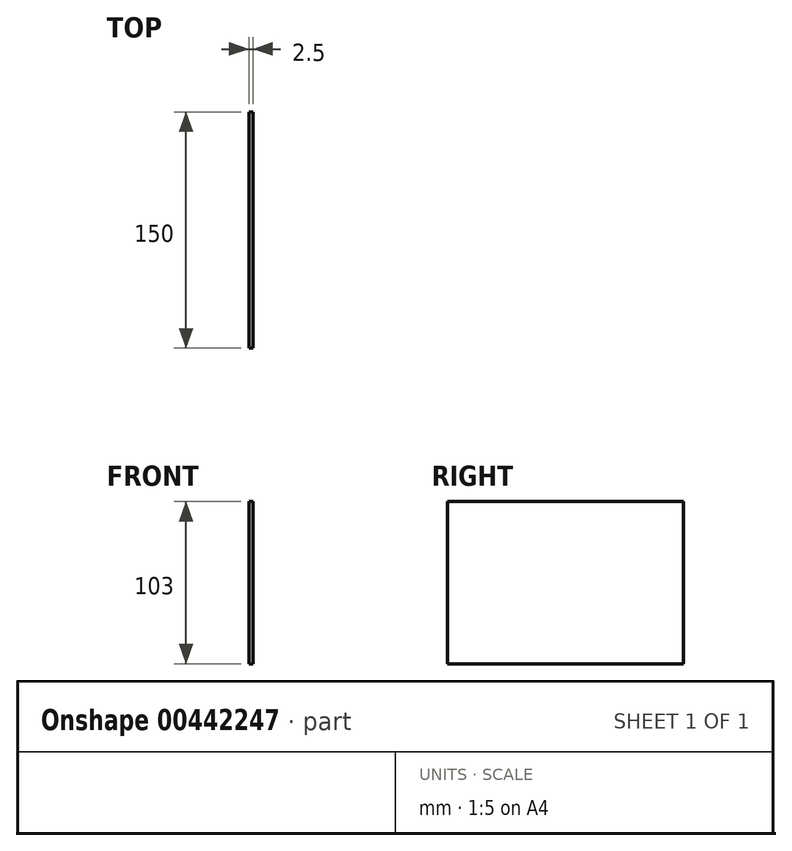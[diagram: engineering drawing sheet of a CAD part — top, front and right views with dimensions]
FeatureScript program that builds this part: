
annotation { "Feature Type Name" : "Feature", "Feature Type Description" : "" }
export const myFeature = defineFeature(function(context is Context, id is Id, definition is map)
    precondition{}
    {
        {
            var Q0;
            Q0=qCreatedBy(makeId("Front.planeOp"),FACE);
            var sketch = newSketch(context, id + "F0", { "sketchPlane" : qUnion([Q0])});
            skLineSegment(sketch, "E0.bottom", {"start": v(-1.25, 51.5) * mm, "end": v(1.25, 51.5) * mm});
            skLineSegment(sketch, "E0.top", {"start": v(-1.25, -51.5) * mm, "end": v(1.25, -51.5) * mm});
            skLineSegment(sketch, "E0.left", {"start": v(-1.25, 51.5) * mm, "end": v(-1.25, -51.5) * mm});
            skLineSegment(sketch, "E0.right", {"start": v(1.25, 51.5) * mm, "end": v(1.25, -51.5) * mm});
            skPoint(sketch, "E0.middle", {"position": v(0, 0) * mm});
            skSolve(sketch);
        }
        {
            var Q0;
            Q0 = qSketchRegion(id + "F0", true);
            extrude(context, id + "F1", {"entities" : qUnion([Q0]), "depth" : 150 * mm});
        }
    });
